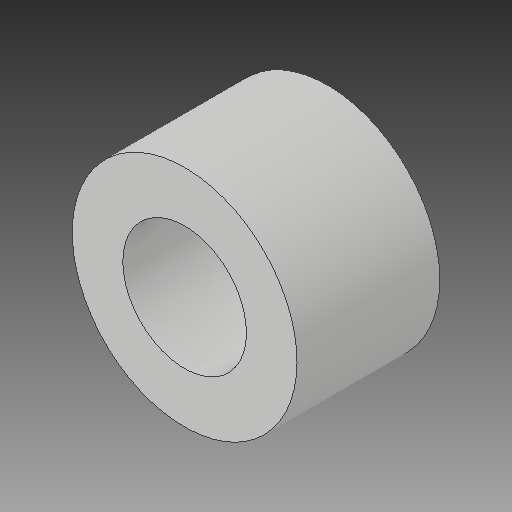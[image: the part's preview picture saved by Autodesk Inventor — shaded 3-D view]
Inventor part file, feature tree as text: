
AUTODESK INVENTOR PART (.ipt)
format: ipt  version: 2017 (Build 210142000, 142)  size: 100,864 bytes
history: native  units: mm
features: other x3, sketch x1
ambient origin geometry x8: Origin, YZ Plane, XZ Plane, XY Plane, X Axis, Y Axis, Z Axis, Center Point
bodies: Solid1 (feature_tree)
feature tree (4):
  other  "Small-Aluminium-Spacer_MIR1.ipt"
  other  "Solid1::Small-Aluminium-Spacer_MIR1.ipt"
  other  "TaggingFeature1"
  sketch  "Sketch1"  dims[d0=10.0mm]
